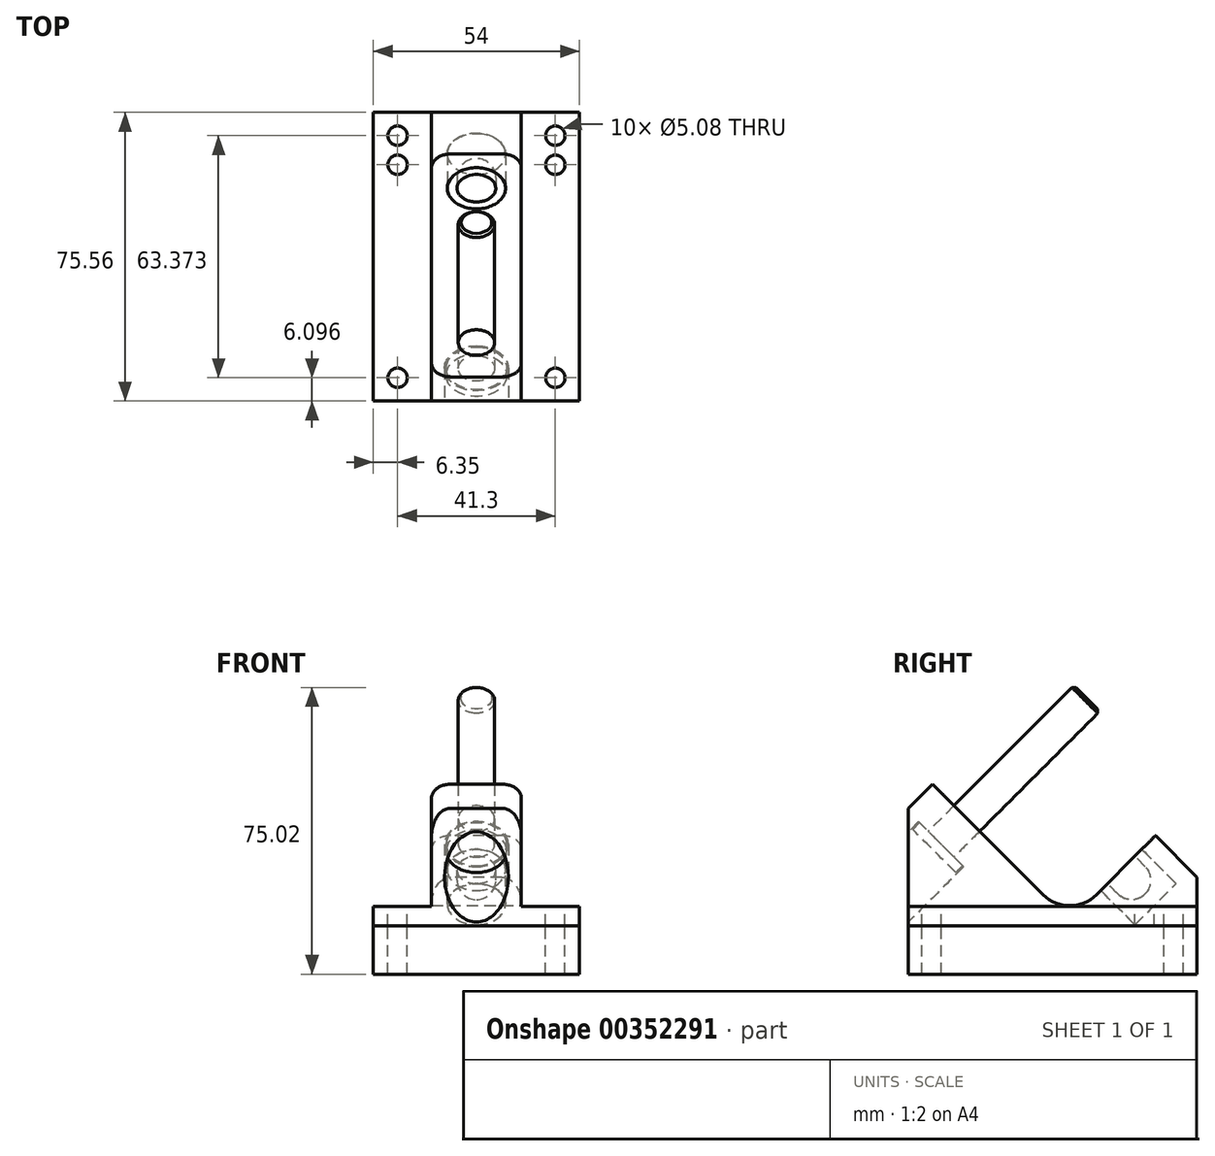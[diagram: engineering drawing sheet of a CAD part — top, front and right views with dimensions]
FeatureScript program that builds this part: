
annotation { "Feature Type Name" : "Feature", "Feature Type Description" : "" }
export const myFeature = defineFeature(function(context is Context, id is Id, definition is map)
    precondition{}
    {
        {
            var Q0;
            Q0=qCreatedBy(makeId("Right.planeOp"),FACE);
            var sketch = newSketch(context, id + "F0", { "sketchPlane" : qUnion([Q0])});
            skLineSegment(sketch, "E0", {"start": v(0, 0) * mm, "end": v(0, 30.72) * mm});
            skLineSegment(sketch, "E1", {"start": v(0, 30.72) * mm, "end": v(6.32, 37.04) * mm});
            skLineSegment(sketch, "E2", {"start": v(6.32, 37.04) * mm, "end": v(42.25, 1.12) * mm});
            skLineSegment(sketch, "E3", {"start": v(42.25, 1.12) * mm, "end": v(64.7, 23.57) * mm});
            skLineSegment(sketch, "E4", {"start": v(64.7, 23.57) * mm, "end": v(75.57, 12.7) * mm});
            skLineSegment(sketch, "E5", {"start": v(75.57, 12.7) * mm, "end": v(75.57, 0) * mm});
            skLineSegment(sketch, "E6", {"start": v(75.57, 0) * mm, "end": v(0, 0) * mm});
            skLineSegment(sketch, "E7", {"start": v(15.3, 28.06) * mm, "end": v(28.77, 41.53) * mm, "construction": true});
            skLineSegment(sketch, "E8", {"start": v(28.77, 41.53) * mm, "end": v(64.7, 5.6) * mm, "construction": true});
            skLineSegment(sketch, "E9", {"start": v(64.7, 5.6) * mm, "end": v(70.08, 11) * mm, "construction": true});
            skLineSegment(sketch, "E10", {"start": v(70.08, 11) * mm, "end": v(61.1, 19.98) * mm, "construction": true});
            skLineSegment(sketch, "E11", {"start": v(28.77, 41.53) * mm, "end": v(15.3, 55) * mm, "construction": true});
            skCircle(sketch, "E12", {"center": v(15.3, 55) * mm, "radius": 4 * mm, "construction": true});
            skLineSegment(sketch, "E13", {"start": v(64.7, 5.6) * mm, "end": v(59.3, 0.22) * mm, "construction": true});
            skLineSegment(sketch, "E14", {"start": v(59.3, 0.22) * mm, "end": v(50.33, 9.2) * mm, "construction": true});
            skCircle(sketch, "E15", {"center": v(58.4, 11.9) * mm, "radius": 5.08 * mm, "construction": true});
            skSolve(sketch);
        }
        {
            var Q0;
            Q0 = qSketchRegion(id + "F0", true);
            extrude(context, id + "F1", {"entities" : qUnion([Q0]), "depth" : 27 * mm});
        }
        {
            var Q0;
            Q0=makeQuery(id+"F1.opExtrude","SWEPT_EDGE",EDGE,{"disambiguationData":[OSD([sQuery(id+"F0.wireOp",EDGE,"E2"),sQuery(id+"F0.wireOp",EDGE,"E3")])]});
            fillet(context, id + "F2", {"entities" : qUnion([Q0]), "radius" : 9.9 * mm, "tangentPropagation" : true, "allowEdgeOverflow" : false});
        }
        {
            var Q0;
            Q0=makeQuery(id+"F1.opExtrude","CAP_FACE",FACE,{"disambiguationData":[OSD([sQuery(id+"F0.wireOp",EDGE,"E0"),sQuery(id+"F0.wireOp",EDGE,"E1"),sQuery(id+"F0.wireOp",EDGE,"E2"),sQuery(id+"F0.wireOp",EDGE,"E3"),sQuery(id+"F0.wireOp",EDGE,"E4"),sQuery(id+"F0.wireOp",EDGE,"E5"),sQuery(id+"F0.wireOp",EDGE,"E6")])],"isStart":false});
            var sketch = newSketch(context, id + "F3", { "sketchPlane" : qUnion([Q0])});
            skLineSegment(sketch, "E16.bottom", {"start": v(0, 5.08) * mm, "end": v(75.57, 5.08) * mm});
            skLineSegment(sketch, "E16.top", {"start": v(0, 37.04) * mm, "end": v(75.57, 37.04) * mm});
            skLineSegment(sketch, "E16.left", {"start": v(0, 5.08) * mm, "end": v(0, 37.04) * mm});
            skLineSegment(sketch, "E16.right", {"start": v(75.57, 5.08) * mm, "end": v(75.57, 37.04) * mm});
            skSolve(sketch);
        }
        {
            var Q0;
            Q0 = qSketchRegion(id + "F3", true);
            extrude(context, id + "F4", {"entities" : qUnion([Q0]), "operationType" : NewBodyOperationType.REMOVE, "oppositeDirection" : true, "depth" : 15.24 * mm});
        }
        {
            var Q0;
            Q0=makeQuery(id+"F4.boolean.opBoolean","COPY",FACE,{"derivedFrom":makeQuery(id+"F4.opExtrude","SWEPT_FACE",FACE,{"disambiguationData":[OSD([sQuery(id+"F3.wireOp",EDGE,"E16.bottom")])]})});
            var sketch = newSketch(context, id + "F5", { "sketchPlane" : qUnion([Q0])});
            skLineSegment(sketch, "E17", {"start": v(20.65, 69.47) * mm, "end": v(20.65, 61.85) * mm, "construction": true});
            skLineSegment(sketch, "E18", {"start": v(20.65, 61.85) * mm, "end": v(20.65, 6.1) * mm, "construction": true});
            skCircle(sketch, "E19", {"center": v(20.65, 69.47) * mm, "radius": 2.54 * mm});
            skCircle(sketch, "E20", {"center": v(20.65, 61.85) * mm, "radius": 2.54 * mm});
            skCircle(sketch, "E21", {"center": v(20.65, 6.1) * mm, "radius": 2.54 * mm});
            skSolve(sketch);
        }
        {
            var Q0;
            Q0 = qSketchRegion(id + "F5", true);
            extrude(context, id + "F6", {"entities" : qUnion([Q0]), "operationType" : NewBodyOperationType.REMOVE, "endBound" : BoundingType.THROUGH_ALL, "oppositeDirection" : true, "depth" : 25.4 * mm});
        }
        {
            var Q0;
            Q0=makeQuery(id+"F1.opExtrude","SWEPT_BODY",BODY,{"disambiguationData":[OSD([sQuery(id+"F0.wireOp",EDGE,"E0"),sQuery(id+"F0.wireOp",EDGE,"E1"),sQuery(id+"F0.wireOp",EDGE,"E2"),sQuery(id+"F0.wireOp",EDGE,"E3"),sQuery(id+"F0.wireOp",EDGE,"E4"),sQuery(id+"F0.wireOp",EDGE,"E5"),sQuery(id+"F0.wireOp",EDGE,"E6")])]});
            var Q1;
            Q1=makeQuery(id+"F1.opExtrude","CAP_FACE",FACE,{"disambiguationData":[OSD([sQuery(id+"F0.wireOp",EDGE,"E0"),sQuery(id+"F0.wireOp",EDGE,"E1"),sQuery(id+"F0.wireOp",EDGE,"E2"),sQuery(id+"F0.wireOp",EDGE,"E3"),sQuery(id+"F0.wireOp",EDGE,"E4"),sQuery(id+"F0.wireOp",EDGE,"E5"),sQuery(id+"F0.wireOp",EDGE,"E6")])],"isStart":true});
            mirror(context, id + "F7", {"operationType" : NewBodyOperationType.ADD, "entities" : qUnion([Q0]), "mirrorPlane" : qUnion([Q1])});
        }
        {
            var Q0;
            Q0=makeQuery(id+"F7.opPattern","COPY",EDGE,{"derivedFrom":makeQuery(id+"F4.boolean.opBoolean","INTERSECT",EDGE,{"derivedFrom":[makeQuery(id+"F1.opExtrude","SWEPT_FACE",FACE,{"disambiguationData":[OSD([sQuery(id+"F0.wireOp",EDGE,"E4")])]}),makeQuery(id+"F4.opExtrude","CAP_FACE",FACE,{"disambiguationData":[OSD([sQuery(id+"F3.wireOp",EDGE,"E16.bottom"),sQuery(id+"F3.wireOp",EDGE,"E16.top"),sQuery(id+"F3.wireOp",EDGE,"E16.left"),sQuery(id+"F3.wireOp",EDGE,"E16.right")])],"isStart":false})]}),"instanceName":"1"});
            var Q1;
            Q1=makeQuery(id+"F4.boolean.opBoolean","INTERSECT",EDGE,{"derivedFrom":[makeQuery(id+"F1.opExtrude","SWEPT_FACE",FACE,{"disambiguationData":[OSD([sQuery(id+"F0.wireOp",EDGE,"E4")])]}),makeQuery(id+"F4.opExtrude","CAP_FACE",FACE,{"disambiguationData":[OSD([sQuery(id+"F3.wireOp",EDGE,"E16.bottom"),sQuery(id+"F3.wireOp",EDGE,"E16.top"),sQuery(id+"F3.wireOp",EDGE,"E16.left"),sQuery(id+"F3.wireOp",EDGE,"E16.right")])],"isStart":false})]});
            var Q2;
            Q2=makeQuery(id+"F4.boolean.opBoolean","INTERSECT",EDGE,{"derivedFrom":[makeQuery(id+"F1.opExtrude","SWEPT_FACE",FACE,{"disambiguationData":[OSD([sQuery(id+"F0.wireOp",EDGE,"E1")])]}),makeQuery(id+"F4.opExtrude","CAP_FACE",FACE,{"disambiguationData":[OSD([sQuery(id+"F3.wireOp",EDGE,"E16.bottom"),sQuery(id+"F3.wireOp",EDGE,"E16.top"),sQuery(id+"F3.wireOp",EDGE,"E16.left"),sQuery(id+"F3.wireOp",EDGE,"E16.right")])],"isStart":false})]});
            var Q3;
            Q3=makeQuery(id+"F7.opPattern","COPY",EDGE,{"derivedFrom":makeQuery(id+"F4.boolean.opBoolean","INTERSECT",EDGE,{"derivedFrom":[makeQuery(id+"F1.opExtrude","SWEPT_FACE",FACE,{"disambiguationData":[OSD([sQuery(id+"F0.wireOp",EDGE,"E1")])]}),makeQuery(id+"F4.opExtrude","CAP_FACE",FACE,{"disambiguationData":[OSD([sQuery(id+"F3.wireOp",EDGE,"E16.bottom"),sQuery(id+"F3.wireOp",EDGE,"E16.top"),sQuery(id+"F3.wireOp",EDGE,"E16.left"),sQuery(id+"F3.wireOp",EDGE,"E16.right")])],"isStart":false})]}),"instanceName":"1"});
            fillet(context, id + "F8", {"entities" : qUnion([Q0, Q1, Q2, Q3]), "radius" : 5.08 * mm, "tangentPropagation" : true, "allowEdgeOverflow" : false});
        }
        {
            var Q0;
            Q0=qCreatedBy(makeId("Right.planeOp"),FACE);
            var sketch = newSketch(context, id + "F9", { "sketchPlane" : qUnion([Q0])});
            skLineSegment(sketch, "E22.0", {"start": v(15.3, 28.06) * mm, "end": v(28.77, 41.53) * mm, "construction": true});
            skLineSegment(sketch, "E22.1", {"start": v(6.32, 37.04) * mm, "end": v(42.25, 1.12) * mm});
            skLineSegment(sketch, "E23", {"start": v(11.94, 31.43) * mm, "end": v(5.2, 24.7) * mm});
            skLineSegment(sketch, "E24", {"start": v(5.2, 24.7) * mm, "end": v(2.67, 27.22) * mm});
            skLineSegment(sketch, "E25", {"start": v(2.67, 27.22) * mm, "end": v(-12.28, 12.28) * mm});
            skLineSegment(sketch, "E26", {"start": v(-12.28, 12.28) * mm, "end": v(-6.38, 6.38) * mm});
            skLineSegment(sketch, "E27", {"start": v(-6.38, 6.38) * mm, "end": v(15.3, 28.06) * mm});
            skLineSegment(sketch, "E28", {"start": v(-6.38, 6.38) * mm, "end": v(0, 0) * mm, "construction": true});
            skSolve(sketch);
        }
        {
            var Q0;
            Q0 = qSketchRegion(id + "F9", true);
            var Q1;
            Q1=sQuery(id+"F9.wireOp",EDGE,"E22.0");
            revolve(context, id + "F10", {"operationType" : NewBodyOperationType.REMOVE, "entities" : qUnion([Q0]), "axis" : qUnion([Q1]), "revolveType" : RevolveType.FULL});
        }
        {
            var Q0;
            Q0=qCreatedBy(makeId("Right.planeOp"),FACE);
            var sketch = newSketch(context, id + "F11", { "sketchPlane" : qUnion([Q0])});
            skLineSegment(sketch, "E29.1", {"start": v(5.2, 24.7) * mm, "end": v(2.95, 26.95) * mm});
            skLineSegment(sketch, "E29.2", {"start": v(11.94, 31.43) * mm, "end": v(5.2, 24.7) * mm});
            skLineSegment(sketch, "E30", {"start": v(2.95, 26.95) * mm, "end": v(1.15, 25.15) * mm});
            skLineSegment(sketch, "E31", {"start": v(1.15, 25.15) * mm, "end": v(6.77, 19.53) * mm});
            skLineSegment(sketch, "E32", {"start": v(6.77, 19.53) * mm, "end": v(46.74, 59.5) * mm});
            skPoint(sketch, "E29.0.end.orphan", {"position": v(-12.28, 12.28) * mm});
            skPoint(sketch, "E29.0.start.orphan", {"position": v(2.67, 27.22) * mm});
            skLineSegment(sketch, "E33", {"start": v(11.94, 31.43) * mm, "end": v(43.37, 62.86) * mm});
            skLineSegment(sketch, "E34", {"start": v(43.37, 62.86) * mm, "end": v(46.74, 59.5) * mm});
            skSolve(sketch);
        }
        {
            var Q0;
            Q0 = qSketchRegion(id + "F11", true);
            var Q1;
            Q1=sQuery(id+"F11.wireOp",EDGE,"E32");
            revolve(context, id + "F12", {"entities" : qUnion([Q0]), "axis" : qUnion([Q1]), "revolveType" : RevolveType.FULL});
        }
        {
            var Q0;
            Q0 = qSketchRegion(id + "F11", true);
            var Q1;
            Q1=sQuery(id+"F0.wireOp",EDGE,"E7");
            revolve(context, id + "F13", {"entities" : qUnion([Q0]), "axis" : qUnion([Q1]), "revolveType" : RevolveType.FULL});
        }
        {
            var Q0;
            Q0=makeQuery(id+"F13.opRevolve","SWEPT_BODY",BODY,{"disambiguationData":[OSD([sQuery(id+"F11.wireOp",EDGE,"E29.1"),sQuery(id+"F11.wireOp",EDGE,"E29.2"),sQuery(id+"F11.wireOp",EDGE,"E30"),sQuery(id+"F11.wireOp",EDGE,"E31"),sQuery(id+"F11.wireOp",EDGE,"E32"),sQuery(id+"F11.wireOp",EDGE,"E33"),sQuery(id+"F11.wireOp",EDGE,"E34")])]});
            deleteBodies(context, id + "F14", {"entities" : qUnion([Q0])});
        }
        {
            var Q0;
            Q0=makeQuery(id+"F12.opRevolve","SWEPT_EDGE",EDGE,{"disambiguationData":[OSD([sQuery(id+"F11.wireOp",EDGE,"E33"),sQuery(id+"F11.wireOp",EDGE,"E34")])]});
            chamfer(context, id + "F15", {"entities" : qUnion([Q0]), "width" : 0.76 * mm, "tangentPropagation" : true});
        }
        {
            var Q0;
            Q0=qCreatedBy(makeId("Right.planeOp"),FACE);
            var sketch = newSketch(context, id + "F16", { "sketchPlane" : qUnion([Q0])});
            skLineSegment(sketch, "E35.0", {"start": v(64.7, 5.6) * mm, "end": v(70.08, 11) * mm});
            skLineSegment(sketch, "E35.1", {"start": v(70.08, 11) * mm, "end": v(61.1, 19.98) * mm, "construction": true});
            skLineSegment(sketch, "E35.2", {"start": v(28.77, 41.53) * mm, "end": v(64.7, 5.6) * mm, "construction": true});
            skLineSegment(sketch, "E36", {"start": v(61.1, 19.98) * mm, "end": v(70.08, 11) * mm});
            skLineSegment(sketch, "E37", {"start": v(64.7, 5.6) * mm, "end": v(55.72, 14.59) * mm});
            skLineSegment(sketch, "E38.0", {"start": v(42.25, 1.12) * mm, "end": v(64.7, 23.57) * mm, "construction": true});
            skLineSegment(sketch, "E39", {"start": v(55.72, 14.59) * mm, "end": v(61.1, 19.98) * mm});
            skSolve(sketch);
        }
        {
            var Q0;
            Q0 = qSketchRegion(id + "F16", true);
            var Q1;
            Q1=sQuery(id+"F16.wireOp",EDGE,"E35.2");
            revolve(context, id + "F17", {"operationType" : NewBodyOperationType.REMOVE, "entities" : qUnion([Q0]), "axis" : qUnion([Q1]), "revolveType" : RevolveType.FULL, "oppositeDirection" : true});
        }
        {
            var Q0;
            Q0=qCreatedBy(makeId("Right.planeOp"),FACE);
            var sketch = newSketch(context, id + "F18", { "sketchPlane" : qUnion([Q0])});
            skLineSegment(sketch, "E40.1", {"start": v(42.25, 1.12) * mm, "end": v(55.72, 14.59) * mm});
            skLineSegment(sketch, "E40.2", {"start": v(70.08, 11) * mm, "end": v(61.1, 19.98) * mm});
            skLineSegment(sketch, "E40.3", {"start": v(64.7, 5.6) * mm, "end": v(70.08, 11) * mm});
            skLineSegment(sketch, "E41.trimOffspring", {"start": v(59.3, 18.18) * mm, "end": v(64.7, 23.57) * mm});
            skLineSegment(sketch, "E42.trimOffspring", {"start": v(62, 8.3) * mm, "end": v(64.7, 5.6) * mm});
            skPoint(sketch, "E40.4.start.orphan", {"position": v(28.77, 41.53) * mm});
            skLineSegment(sketch, "E43", {"start": v(59.3, 18.18) * mm, "end": v(61.1, 19.98) * mm});
            skLineSegment(sketch, "E44", {"start": v(70.08, 11) * mm, "end": v(64.7, 5.6) * mm});
            skCircle(sketch, "E45.0", {"center": v(58.4, 11.9) * mm, "radius": 5.08 * mm, "construction": true});
            skArc(sketch, "E46", {"start": v(62, 8.3) * mm, "mid": v(63.49, 11.9) * mm, "end": v(62, 15.49) * mm});
            skLineSegment(sketch, "E47", {"start": v(59.3, 18.18) * mm, "end": v(62, 15.49) * mm});
            skSolve(sketch);
        }
        {
            var Q0;
            Q0 = qSketchRegion(id + "F18", true);
            var Q1;
            Q1=sQuery(id+"F0.wireOp",EDGE,"E8");
            revolve(context, id + "F19", {"entities" : qUnion([Q0]), "axis" : qUnion([Q1]), "revolveType" : RevolveType.FULL});
        }
        {
            var Q0;
            {var subQ0=makeQuery(id+"F1.opExtrude","SWEPT_FACE",FACE,{"disambiguationData":[OSD([sQuery(id+"F0.wireOp",EDGE,"E6")])]});Q0=makeQuery(id+"F7.boolean.opBoolean","MERGE",FACE,{"derivedFrom":[subQ0,makeQuery(id+"F7.opPattern","COPY",FACE,{"derivedFrom":subQ0,"instanceName":"1"})]});}
            var sketch = newSketch(context, id + "F20", { "sketchPlane" : qUnion([Q0])});
            skCircle(sketch, "E48.0", {"center": v(-20.65, -6.1) * mm, "radius": 2.54 * mm});
            skCircle(sketch, "E48.1", {"center": v(20.65, -6.1) * mm, "radius": 2.54 * mm});
            skCircle(sketch, "E48.2", {"center": v(-20.65, -69.47) * mm, "radius": 2.54 * mm});
            skCircle(sketch, "E48.3", {"center": v(20.65, -69.47) * mm, "radius": 2.54 * mm});
            skLineSegment(sketch, "E49.bottom", {"start": v(-27, 0) * mm, "end": v(27, 0) * mm});
            skLineSegment(sketch, "E49.top", {"start": v(-27, -75.57) * mm, "end": v(27, -75.57) * mm});
            skLineSegment(sketch, "E49.left", {"start": v(-27, 0) * mm, "end": v(-27, -75.57) * mm});
            skLineSegment(sketch, "E49.right", {"start": v(27, 0) * mm, "end": v(27, -75.57) * mm});
            skSolve(sketch);
        }
        {
            var Q0;
            Q0 = qSketchRegion(id + "F20", true);
            extrude(context, id + "F21", {"entities" : qUnion([Q0]), "depth" : 12.7 * mm});
        }
    });
